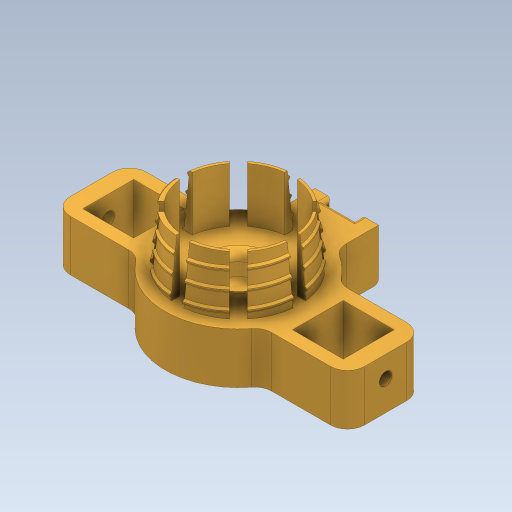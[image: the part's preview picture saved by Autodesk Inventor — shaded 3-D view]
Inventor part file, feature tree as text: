
AUTODESK INVENTOR PART (.ipt)
format: ipt  version: 2023 (Build 270158000, 158)  size: 1,005,568 bytes
history: native  units: mm
features: sketch x8, extrude x5, hole x3, fillet x3, helix x2, direct_edit x2, draft x1, mirror x1, other x1, revolve x1
ambient origin geometry x8: Origin, YZ Plane, XZ Plane, XY Plane, X Axis, Y Axis, Z Axis, Center Point
bodies: Solid1 (feature_tree)
feature tree (27):
  extrude  "Extrusion1"  Depth=12.875mm
  draft  "FaceDraft1"
  sketch  "Sketch2"  dims[d34=0.0mm d35=0.0mm d56=8.726646mm]
  helix  "Coil3"  [1 undecoded]
  helix  "Coil4"  [1 undecoded]
  direct_edit  "Direct Edit2"
  extrude  "Extrusion2"  Depth=8.726646mm
  extrude  "Extrusion13"  TaperAngle=90.0deg  [1 undecoded]
  extrude  "Extrusion14"  Depth=34.58632mm
  hole  "Hole3"  [1 undecoded]
  hole  "Hole4"  [1 undecoded]
  fillet  "Fillet11"  Radius=3.0mm
  fillet  "Fillet12"  Radius=80.0mm
  hole  "Hole5"  [1 undecoded]
  mirror  "Mirror2"
  extrude  "Extrusion15"  Depth=1.0mm
  direct_edit  "Direct Edit3"
  fillet  "Fillet13"  Radius=18.0mm
  sketch  "Sketch1"  dims[d0=25.0mm d1=26.5mm d2=12.875mm d3=0.0mm d4=1.047198mm]
  sketch  "Sketch3"  dims[d62=4.0mm d63=13.0mm d64=10.0mm d65=1.047198mm]
  sketch  "Sketch11"  dims[d66=90.0deg d67=90.0deg d68=0.0mm d69=0.0mm d70=4.0mm d71=3.0mm d72=10.0mm d73=-1.047198mm d74=90.0deg d75=90.0deg d76=0.0mm d77=0.0mm]
  sketch  "Sketch13"  dims[d79=-0.127mm d145=34.58632mm]
  sketch  "Sketch14"  dims[d150=120.0deg d151=120.0deg]
  sketch  "Sketch15"  dims[d153=21.6866mm d157=12.0mm d158=0.0mm d159=3.0mm d160=80.0mm d162=360.0deg]
  sketch  "Sketch16"  dims[d164=0.0mm d165=0.0mm d179=5.3mm d180=6.0mm d181=4.0mm d182=2.0mm d183=90.0deg d184=5.0mm d185=0.0mm d186=10.0mm d187=6.0mm d188=4.0mm d189=2.0mm d190=90.0deg d191=7.0mm d192=0.0mm d193=2.0mm d194=20.0mm d195=18.0mm d196=12.0mm d197=10.0mm d198=4.0mm d199=3.0mm d200=6.0mm d201=3.01mm d202=2.0mm d203=14.3117mm d204=8.0mm d205=0.0mm d206=15.0mm d207=10.0mm d208=7.0mm d209=10.0mm d210=1.0mm d211=0.0mm d212=-4.363323mm d213=1.0mm d109=0.5mm d110=0.872665mm d111=0.5mm d112=0.872665mm]
  other  "Size2"
  revolve  "Rotate1"  [1 undecoded]
note: 7 required parameter values undecoded (feature->parameter linkage not recoverable at this tier; creation-order binding heuristic only, values carry confidence <= 0.55)